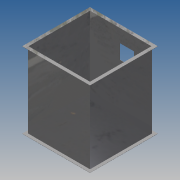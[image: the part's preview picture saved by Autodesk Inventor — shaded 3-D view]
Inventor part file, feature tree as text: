
AUTODESK INVENTOR PART (.ipt)
format: ipt  version: 2014 SP1 (Build 180222100, 222)  size: 171,520 bytes
history: native  units: in
note: dims shown in document units (in); Inventor stores cm internally (conversion verified against a paired STEP export)
features: sketch x8, extrude x7, hole x1, other x1
ambient origin geometry x8: Origin, YZ Plane, XZ Plane, XY Plane, X Axis, Y Axis, Z Axis, Center Point
bodies: Solid1 (feature_tree)
feature tree (17):
  extrude  "Extrusion1"  Depth=33.4646in
  extrude  "Extrusion2"  Depth=1.5748in
  extrude  "Extrusion3"  Depth=0.1in
  extrude  "Extrusion4"  Depth=1.4764in TaperAngle=0.0deg
  extrude  "Extrusion5"  Depth=0.1in
  hole  "Hole1"  [1 undecoded]
  extrude  "Extrusion6"  Depth=1.4764in TaperAngle=0.0deg
  extrude  "Extrusion8"  Depth=1.0in
  other  "Power"
  sketch  "Sketch1"  dims[d0=33.4646in d1=33.4646in]
  sketch  "Sketch2"  dims[d2=37.4016in d3=0.0in d4=1.5748in]
  sketch  "Sketch3"  dims[d5=39.3701in d6=0.0in d7=0.1in]
  sketch  "Sketch4"  dims[d8=0.1in d9=1.4764in d10=0.0in]
  sketch  "Sketch5"  dims[d11=0.1in d12=0.1in]
  sketch  "Sketch6"  dims[d13=1.4764in d14=0.0in d15=1.4764in]
  sketch  "Sketch7"  dims[d16=1.4764in d17=39.3701in d18=0.0in]
  sketch  "Sketch9"  dims[d19=0.5906in d20=0.5906in d21=0.7874in d23=26.378in d24=0.7874in d26=26.378in d29=0.25in d30=0.75in d31=0.375in d32=0.25in d33=0.5635in d34=1.0in d35=0.8108in d36=8.6614in d37=7.0866in d38=7.0866in d39=0.3937in d40=0.0in d48=1.5in d49=2.0in d50=1.0in d51=0.0in]
note: 1 required parameter value undecoded (feature->parameter linkage not recoverable at this tier; creation-order binding heuristic only, values carry confidence <= 0.55)
